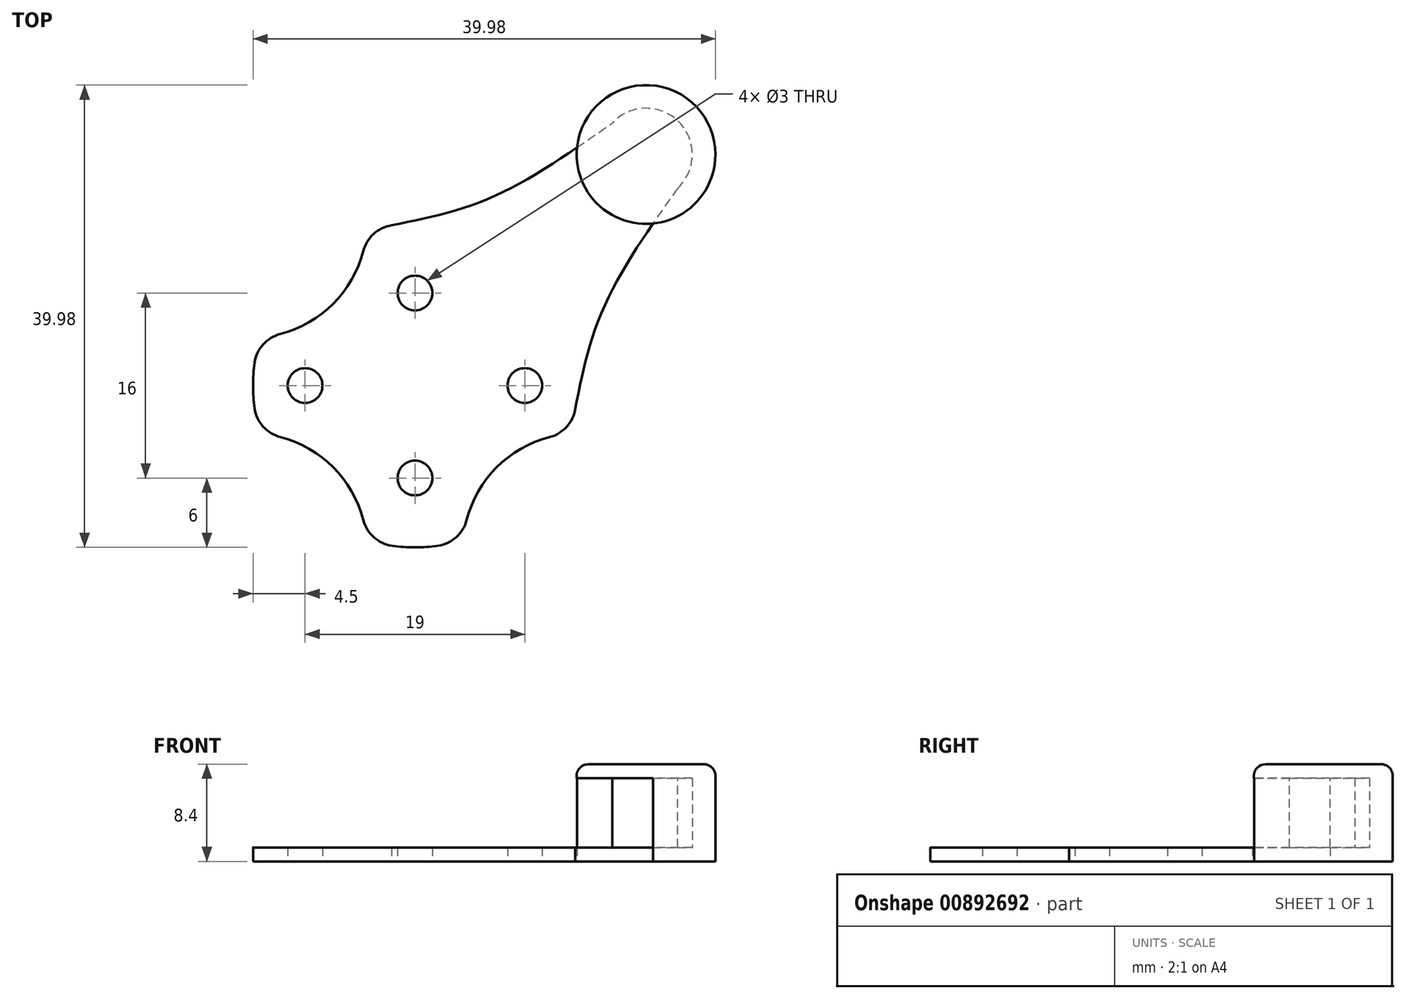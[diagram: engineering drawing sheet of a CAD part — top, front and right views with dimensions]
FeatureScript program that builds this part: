
annotation { "Feature Type Name" : "Feature", "Feature Type Description" : "" }
export const myFeature = defineFeature(function(context is Context, id is Id, definition is map)
    precondition{}
    {
        {
            var Q0;
            Q0=qCreatedBy(makeId("Top.planeOp"),FACE);
            var sketch = newSketch(context, id + "F0", { "sketchPlane" : qUnion([Q0])});
            skArc(sketch, "E0", {"start": v(-13.36, 4.17) * mm, "mid": v(-14, 0) * mm, "end": v(-13.36, -4.17) * mm});
            skCircle(sketch, "E1", {"center": v(19.98, 19.98) * mm, "radius": 4 * mm});
            skCircle(sketch, "E2", {"center": v(19.98, 19.98) * mm, "radius": 6 * mm});
            skCircle(sketch, "E3", {"center": v(9.5, 0) * mm, "radius": 1.5 * mm});
            skCircle(sketch, "E4", {"center": v(0, 8) * mm, "radius": 1.5 * mm});
            skCircle(sketch, "E5", {"center": v(-9.5, 0) * mm, "radius": 1.5 * mm});
            skCircle(sketch, "E6", {"center": v(0, -8) * mm, "radius": 1.5 * mm});
            skFitSpline(sketch, "E7", {"points": [v(17.05, 22.7) * mm, v(6.68, 16.3) * mm, v(-2.02, 13.85) * mm], "startDerivative": vector(-19.43, -13.68) * mm, "endDerivative": vector(-18.68, -3.78) * mm});
            skFitSpline(sketch, "E8.MirrorCS", {"points": [v(22.7, 17.05) * mm, v(16.3, 6.68) * mm, v(13.85, -2.02) * mm], "startDerivative": vector(-13.68, -19.43) * mm, "endDerivative": vector(-3.78, -18.68) * mm});
            skArc(sketch, "E9", {"start": v(-4.17, -13.36) * mm, "mid": v(-7.07, -7.07) * mm, "end": v(-13.36, -4.17) * mm});
            skArc(sketch, "E10", {"start": v(-13.36, 4.17) * mm, "mid": v(-7.07, 7.07) * mm, "end": v(-4.17, 13.36) * mm});
            skArc(sketch, "E11", {"start": v(13.36, -4.17) * mm, "mid": v(7.07, -7.07) * mm, "end": v(4.17, -13.36) * mm});
            skArc(sketch, "E12.trimOffspring", {"start": v(-4.17, -13.36) * mm, "mid": v(0, -14) * mm, "end": v(4.17, -13.36) * mm});
            skArc(sketch, "E13.trimOffspring", {"start": v(13.36, -4.17) * mm, "mid": v(13.65, -3.1) * mm, "end": v(13.85, -2.02) * mm});
            skArc(sketch, "E14.trimOffspring", {"start": v(-2.02, 13.85) * mm, "mid": v(-3.1, 13.65) * mm, "end": v(-4.17, 13.36) * mm});
            skCircle(sketch, "E15", {"center": v(-9.5, 0) * mm, "radius": 3 * mm});
            skCircle(sketch, "E16", {"center": v(0, 8) * mm, "radius": 3 * mm});
            skCircle(sketch, "E17", {"center": v(9.5, 0) * mm, "radius": 3 * mm});
            skCircle(sketch, "E18", {"center": v(0, -8) * mm, "radius": 3 * mm});
            skSolve(sketch);
        }
        {
            var Q0;
            Q0=qSketchRegion(id+"F0",true);
            var Q1;
            {var subQ0=sQuery(id+"F0.wireOp",EDGE,"E1");var subQ1=makeQuery(id+"F0.imprint","INTERSECT",VERTEX,{"derivedFrom":[subQ0,sQuery(id+"F0.wireOp",EDGE,"E7")]});Q1=makeQuery(id+"F0.imprint","IMPRINT",FACE,{"disambiguationData":[TD([[makeQuery(id+"F0.imprint","IMPRINT",EDGE,{"disambiguationData":[TD([[subQ1,-1.0]])],"derivedFrom":subQ0}),1.0]])]});}
            var Q2;
            Q2=makeQuery(id+"F0.imprint","IMPRINT",FACE,{"disambiguationData":[TD([[makeQuery(id+"F0.imprint","IMPRINT",EDGE,{"derivedFrom":sQuery(id+"F0.wireOp",EDGE,"E3")}),-1.0]])]});
            var Q3;
            Q3=makeQuery(id+"F0.imprint","IMPRINT",FACE,{"disambiguationData":[TD([[makeQuery(id+"F0.imprint","IMPRINT",EDGE,{"derivedFrom":sQuery(id+"F0.wireOp",EDGE,"E4")}),-1.0]])]});
            var Q4;
            Q4=makeQuery(id+"F0.imprint","IMPRINT",FACE,{"disambiguationData":[TD([[makeQuery(id+"F0.imprint","IMPRINT",EDGE,{"derivedFrom":sQuery(id+"F0.wireOp",EDGE,"E5")}),-1.0]])]});
            var Q5;
            Q5=makeQuery(id+"F0.imprint","IMPRINT",FACE,{"disambiguationData":[TD([[makeQuery(id+"F0.imprint","IMPRINT",EDGE,{"derivedFrom":sQuery(id+"F0.wireOp",EDGE,"E6")}),-1.0]])]});
            extrude(context, id + "F1", {"entities" : qUnion([Q0, Q1, Q2, Q3, Q4, Q5]), "depth" : 1.2 * mm, "offsetDistance" : 25 * mm});
        }
        {
            var Q0;
            {var subQ0=sQuery(id+"F0.wireOp",EDGE,"E7");var subQ1=sQuery(id+"F0.wireOp",EDGE,"E1");var subQ2=makeQuery(id+"F0.imprint","INTERSECT",VERTEX,{"derivedFrom":[subQ1,subQ0]});Q0=makeQuery(id+"F0.imprint","IMPRINT",FACE,{"disambiguationData":[TD([[makeQuery(id+"F0.imprint","IMPRINT",EDGE,{"disambiguationData":[TD([[subQ2,1.0]])],"derivedFrom":subQ1}),-1.0]])]});}
            var Q1;
            {var subQ0=sQuery(id+"F0.wireOp",EDGE,"E1");var subQ1=makeQuery(id+"F0.imprint","INTERSECT",VERTEX,{"derivedFrom":[subQ0,sQuery(id+"F0.wireOp",EDGE,"E7")]});Q1=makeQuery(id+"F0.imprint","IMPRINT",FACE,{"disambiguationData":[TD([[makeQuery(id+"F0.imprint","IMPRINT",EDGE,{"disambiguationData":[TD([[subQ1,-1.0]])],"derivedFrom":subQ0}),1.0]])]});}
            var Q2;
            {var subQ0=sQuery(id+"F0.wireOp",EDGE,"E7");var subQ1=sQuery(id+"F0.wireOp",EDGE,"E1");var subQ2=makeQuery(id+"F0.imprint","INTERSECT",VERTEX,{"derivedFrom":[subQ1,subQ0]});Q2=makeQuery(id+"F0.imprint","IMPRINT",FACE,{"disambiguationData":[TD([[makeQuery(id+"F0.imprint","IMPRINT",EDGE,{"disambiguationData":[TD([[subQ2,-1.0]])],"derivedFrom":subQ1}),-1.0]])]});}
            extrude(context, id + "F2", {"entities" : qUnion([Q0, Q1, Q2]), "operationType" : NewBodyOperationType.ADD, "depth" : 8.4 * mm, "offsetDistance" : 25 * mm});
        }
        {
            var Q0;
            {var subQ0=sQuery(id+"F0.wireOp",EDGE,"E1");var subQ1=makeQuery(id+"F0.imprint","INTERSECT",VERTEX,{"derivedFrom":[subQ0,sQuery(id+"F0.wireOp",EDGE,"E7")]});Q0=makeQuery(id+"F0.imprint","IMPRINT",FACE,{"disambiguationData":[TD([[makeQuery(id+"F0.imprint","IMPRINT",EDGE,{"disambiguationData":[TD([[subQ1,-1.0]])],"derivedFrom":subQ0}),1.0]])]});}
            var Q1;
            {var subQ0=sQuery(id+"F0.wireOp",EDGE,"E7");var subQ1=sQuery(id+"F0.wireOp",EDGE,"E1");var subQ2=makeQuery(id+"F0.imprint","INTERSECT",VERTEX,{"derivedFrom":[subQ1,subQ0]});Q1=makeQuery(id+"F0.imprint","IMPRINT",FACE,{"disambiguationData":[TD([[makeQuery(id+"F0.imprint","IMPRINT",EDGE,{"disambiguationData":[TD([[subQ2,-1.0]])],"derivedFrom":subQ1}),-1.0]])]});}
            extrude(context, id + "F3", {"entities" : qUnion([Q0, Q1]), "operationType" : NewBodyOperationType.REMOVE, "oppositeDirection" : true, "depth" : -7.2 * mm, "offsetDistance" : 25 * mm});
        }
        {
            var Q0;
            {var subQ0=sQuery(id+"F0.wireOp",EDGE,"E1");var subQ1=makeQuery(id+"F0.imprint","INTERSECT",VERTEX,{"derivedFrom":[subQ0,sQuery(id+"F0.wireOp",EDGE,"E7")]});Q0=makeQuery(id+"F0.imprint","IMPRINT",FACE,{"disambiguationData":[TD([[makeQuery(id+"F0.imprint","IMPRINT",EDGE,{"disambiguationData":[TD([[subQ1,-1.0]])],"derivedFrom":subQ0}),1.0]])]});}
            var Q1;
            {var subQ0=sQuery(id+"F0.wireOp",EDGE,"E7");var subQ1=sQuery(id+"F0.wireOp",EDGE,"E1");var subQ2=makeQuery(id+"F0.imprint","INTERSECT",VERTEX,{"derivedFrom":[subQ1,subQ0]});Q1=makeQuery(id+"F0.imprint","IMPRINT",FACE,{"disambiguationData":[TD([[makeQuery(id+"F0.imprint","IMPRINT",EDGE,{"disambiguationData":[TD([[subQ2,-1.0]])],"derivedFrom":subQ1}),-1.0]])]});}
            extrude(context, id + "F4", {"entities" : qUnion([Q0, Q1]), "depth" : 1.2 * mm, "offsetDistance" : 25 * mm});
        }
        {
            var Q0;
            {var subQ0=sQuery(id+"F0.wireOp",EDGE,"E7");var subQ1=sQuery(id+"F0.wireOp",EDGE,"E1");var subQ2=makeQuery(id+"F0.imprint","INTERSECT",VERTEX,{"derivedFrom":[subQ1,subQ0]});Q0=makeQuery(id+"F0.imprint","IMPRINT",FACE,{"disambiguationData":[TD([[makeQuery(id+"F0.imprint","IMPRINT",EDGE,{"disambiguationData":[TD([[subQ2,1.0]])],"derivedFrom":subQ1}),-1.0]])]});}
            var Q1;
            {var subQ0=sQuery(id+"F0.wireOp",EDGE,"E1");var subQ1=makeQuery(id+"F0.imprint","INTERSECT",VERTEX,{"derivedFrom":[subQ0,sQuery(id+"F0.wireOp",EDGE,"E7")]});Q1=makeQuery(id+"F0.imprint","IMPRINT",FACE,{"disambiguationData":[TD([[makeQuery(id+"F0.imprint","IMPRINT",EDGE,{"disambiguationData":[TD([[subQ1,-1.0]])],"derivedFrom":subQ0}),1.0]])]});}
            var Q2;
            {var subQ0=sQuery(id+"F0.wireOp",EDGE,"E7");var subQ1=sQuery(id+"F0.wireOp",EDGE,"E1");var subQ2=makeQuery(id+"F0.imprint","INTERSECT",VERTEX,{"derivedFrom":[subQ1,subQ0]});Q2=makeQuery(id+"F0.imprint","IMPRINT",FACE,{"disambiguationData":[TD([[makeQuery(id+"F0.imprint","IMPRINT",EDGE,{"disambiguationData":[TD([[subQ2,-1.0]])],"derivedFrom":subQ1}),-1.0]])]});}
            extrude(context, id + "F5", {"entities" : qUnion([Q0, Q1, Q2]), "depth" : -1 * mm, "offsetDistance" : 25 * mm});
        }
        {
            var Q0;
            Q0=makeQuery(id+"F5.opExtrude","SWEPT_BODY",BODY,{"disambiguationData":[OSD([sQuery(id+"F0.wireOp",EDGE,"E2")])]});
            deleteBodies(context, id + "F6", {"entities" : qUnion([Q0])});
        }
        {
            var Q0;
            Q0=makeQuery(id+"F3.boolean.opBoolean","SPLIT",BODY,{"disambiguationData":[OD(0.0)],"derivedFrom":makeQuery(id+"F1.opExtrude","SWEPT_BODY",BODY,{"disambiguationData":[OSD([sQuery(id+"F0.wireOp",EDGE,"E0"),sQuery(id+"F0.wireOp",EDGE,"E2"),sQuery(id+"F0.wireOp",EDGE,"E3"),sQuery(id+"F0.wireOp",EDGE,"E4"),sQuery(id+"F0.wireOp",EDGE,"E5"),sQuery(id+"F0.wireOp",EDGE,"E6"),sQuery(id+"F0.wireOp",EDGE,"E7"),sQuery(id+"F0.wireOp",EDGE,"E8.MirrorCS"),sQuery(id+"F0.wireOp",EDGE,"E9"),sQuery(id+"F0.wireOp",EDGE,"E10"),sQuery(id+"F0.wireOp",EDGE,"E11"),sQuery(id+"F0.wireOp",EDGE,"E12.trimOffspring"),sQuery(id+"F0.wireOp",EDGE,"E13.trimOffspring"),sQuery(id+"F0.wireOp",EDGE,"E14.trimOffspring")])]})});
            var Q1;
            Q1=makeQuery(id+"F3.boolean.opBoolean","SPLIT",BODY,{"disambiguationData":[OD(1.0)],"derivedFrom":makeQuery(id+"F1.opExtrude","SWEPT_BODY",BODY,{"disambiguationData":[OSD([sQuery(id+"F0.wireOp",EDGE,"E0"),sQuery(id+"F0.wireOp",EDGE,"E2"),sQuery(id+"F0.wireOp",EDGE,"E3"),sQuery(id+"F0.wireOp",EDGE,"E4"),sQuery(id+"F0.wireOp",EDGE,"E5"),sQuery(id+"F0.wireOp",EDGE,"E6"),sQuery(id+"F0.wireOp",EDGE,"E7"),sQuery(id+"F0.wireOp",EDGE,"E8.MirrorCS"),sQuery(id+"F0.wireOp",EDGE,"E9"),sQuery(id+"F0.wireOp",EDGE,"E10"),sQuery(id+"F0.wireOp",EDGE,"E11"),sQuery(id+"F0.wireOp",EDGE,"E12.trimOffspring"),sQuery(id+"F0.wireOp",EDGE,"E13.trimOffspring"),sQuery(id+"F0.wireOp",EDGE,"E14.trimOffspring")])]})});
            var Q2;
            Q2=makeQuery(id+"F4.opExtrude","SWEPT_BODY",BODY,{"disambiguationData":[OSD([sQuery(id+"F0.wireOp",EDGE,"E1"),sQuery(id+"F0.wireOp",EDGE,"E2"),sQuery(id+"F0.wireOp",EDGE,"E7"),sQuery(id+"F0.wireOp",EDGE,"E8.MirrorCS")])]});
            var Q3;
            Q3=makeQuery(id+"Fnpps8gC1a0rlgX_0.opExtrude","SWEPT_BODY",BODY,{"disambiguationData":[OSD([sQuery(id+"F0.wireOp",EDGE,"E0"),sQuery(id+"F0.wireOp",EDGE,"E2"),sQuery(id+"F0.wireOp",EDGE,"E7"),sQuery(id+"F0.wireOp",EDGE,"E8.MirrorCS"),sQuery(id+"F0.wireOp",EDGE,"E9"),sQuery(id+"F0.wireOp",EDGE,"E10"),sQuery(id+"F0.wireOp",EDGE,"E11"),sQuery(id+"F0.wireOp",EDGE,"E12.trimOffspring"),sQuery(id+"F0.wireOp",EDGE,"E13.trimOffspring"),sQuery(id+"F0.wireOp",EDGE,"E14.trimOffspring"),sQuery(id+"F0.wireOp",EDGE,"E15"),sQuery(id+"F0.wireOp",EDGE,"E16"),sQuery(id+"F0.wireOp",EDGE,"E17"),sQuery(id+"F0.wireOp",EDGE,"E18")])]});
            booleanBodies(context, id + "F7", {"operationType" : BooleanOperationType.UNION, "tools" : qUnion([Q0, Q1, Q2, Q3])});
        }
        {
            var Q0;
            {var subQ0=sQuery(id+"F0.wireOp",EDGE,"E12.trimOffspring");var subQ1=sQuery(id+"F0.wireOp",EDGE,"E11");Q0=makeQuery(id+"F7.opBoolean","MERGE",EDGE,{"derivedFrom":[makeQuery(id+"F1.opExtrude","SWEPT_EDGE",EDGE,{"disambiguationData":[OSD([subQ1,subQ0])]}),makeQuery(id+"Fnpps8gC1a0rlgX_0.opExtrude","SWEPT_EDGE",EDGE,{"disambiguationData":[OSD([subQ1,subQ0])]})]});}
            var Q1;
            {var subQ0=sQuery(id+"F0.wireOp",EDGE,"E12.trimOffspring");var subQ1=sQuery(id+"F0.wireOp",EDGE,"E9");Q1=makeQuery(id+"F7.opBoolean","MERGE",EDGE,{"derivedFrom":[makeQuery(id+"F1.opExtrude","SWEPT_EDGE",EDGE,{"disambiguationData":[OSD([subQ1,subQ0])]}),makeQuery(id+"Fnpps8gC1a0rlgX_0.opExtrude","SWEPT_EDGE",EDGE,{"disambiguationData":[OSD([subQ1,subQ0])]})]});}
            var Q2;
            {var subQ0=sQuery(id+"F0.wireOp",EDGE,"E13.trimOffspring");var subQ1=sQuery(id+"F0.wireOp",EDGE,"E11");Q2=makeQuery(id+"F7.opBoolean","MERGE",EDGE,{"derivedFrom":[makeQuery(id+"F1.opExtrude","SWEPT_EDGE",EDGE,{"disambiguationData":[OSD([subQ1,subQ0])]}),makeQuery(id+"Fnpps8gC1a0rlgX_0.opExtrude","SWEPT_EDGE",EDGE,{"disambiguationData":[OSD([subQ1,subQ0])]})]});}
            var Q3;
            {var subQ0=sQuery(id+"F0.wireOp",EDGE,"E9");var subQ1=sQuery(id+"F0.wireOp",EDGE,"E0");Q3=makeQuery(id+"F7.opBoolean","MERGE",EDGE,{"derivedFrom":[makeQuery(id+"F1.opExtrude","SWEPT_EDGE",EDGE,{"disambiguationData":[OSD([subQ1,subQ0])]}),makeQuery(id+"Fnpps8gC1a0rlgX_0.opExtrude","SWEPT_EDGE",EDGE,{"disambiguationData":[OSD([subQ1,subQ0])]})]});}
            var Q4;
            {var subQ0=sQuery(id+"F0.wireOp",EDGE,"E10");var subQ1=sQuery(id+"F0.wireOp",EDGE,"E0");Q4=makeQuery(id+"F7.opBoolean","MERGE",EDGE,{"derivedFrom":[makeQuery(id+"F1.opExtrude","SWEPT_EDGE",EDGE,{"disambiguationData":[OSD([subQ1,subQ0])]}),makeQuery(id+"Fnpps8gC1a0rlgX_0.opExtrude","SWEPT_EDGE",EDGE,{"disambiguationData":[OSD([subQ1,subQ0])]})]});}
            var Q5;
            {var subQ0=sQuery(id+"F0.wireOp",EDGE,"E14.trimOffspring");var subQ1=sQuery(id+"F0.wireOp",EDGE,"E10");Q5=makeQuery(id+"F7.opBoolean","MERGE",EDGE,{"derivedFrom":[makeQuery(id+"F1.opExtrude","SWEPT_EDGE",EDGE,{"disambiguationData":[OSD([subQ1,subQ0])]}),makeQuery(id+"Fnpps8gC1a0rlgX_0.opExtrude","SWEPT_EDGE",EDGE,{"disambiguationData":[OSD([subQ1,subQ0])]})]});}
            var Q6;
            Q6=makeQuery(id+"F2.opExtrude","CAP_EDGE",EDGE,{"disambiguationData":[OSD([sQuery(id+"F0.wireOp",EDGE,"E2")])],"isStart":false});
            var Q7;
            Q7=makeQuery(id+"Fnpps8gC1a0rlgX_0.opExtrude","CAP_EDGE",EDGE,{"disambiguationData":[OSD([sQuery(id+"F0.wireOp",EDGE,"E2")])],"isStart":false});
            fillet(context, id + "F8", {"entities" : qUnion([Q0, Q1, Q2, Q3, Q4, Q5, Q6, Q7]), "radius" : 1 * mm, "tangentPropagation" : true, "allowEdgeOverflow" : false});
        }
        {
            var Q0;
            Q0=makeQuery(id+"F1.opExtrude","SWEPT_EDGE",EDGE,{"disambiguationData":[OSD([sQuery(id+"F0.wireOp",EDGE,"E9"),sQuery(id+"F0.wireOp",EDGE,"E12.trimOffspring")])]});
            var Q1;
            Q1=makeQuery(id+"F1.opExtrude","SWEPT_EDGE",EDGE,{"disambiguationData":[OSD([sQuery(id+"F0.wireOp",EDGE,"E11"),sQuery(id+"F0.wireOp",EDGE,"E12.trimOffspring")])]});
            var Q2;
            Q2=makeQuery(id+"F1.opExtrude","SWEPT_EDGE",EDGE,{"disambiguationData":[OSD([sQuery(id+"F0.wireOp",EDGE,"E11"),sQuery(id+"F0.wireOp",EDGE,"E13.trimOffspring")])]});
            var Q3;
            Q3=makeQuery(id+"F1.opExtrude","SWEPT_EDGE",EDGE,{"disambiguationData":[OSD([sQuery(id+"F0.wireOp",EDGE,"E10"),sQuery(id+"F0.wireOp",EDGE,"E14.trimOffspring")])]});
            var Q4;
            Q4=makeQuery(id+"F1.opExtrude","SWEPT_EDGE",EDGE,{"disambiguationData":[OSD([sQuery(id+"F0.wireOp",EDGE,"E0"),sQuery(id+"F0.wireOp",EDGE,"E10")])]});
            var Q5;
            Q5=makeQuery(id+"F1.opExtrude","SWEPT_EDGE",EDGE,{"disambiguationData":[OSD([sQuery(id+"F0.wireOp",EDGE,"E0"),sQuery(id+"F0.wireOp",EDGE,"E9")])]});
            fillet(context, id + "F9", {"entities" : qUnion([Q0, Q1, Q2, Q3, Q4, Q5]), "radius" : 3 * mm, "tangentPropagation" : true, "allowEdgeOverflow" : false});
        }
    });
